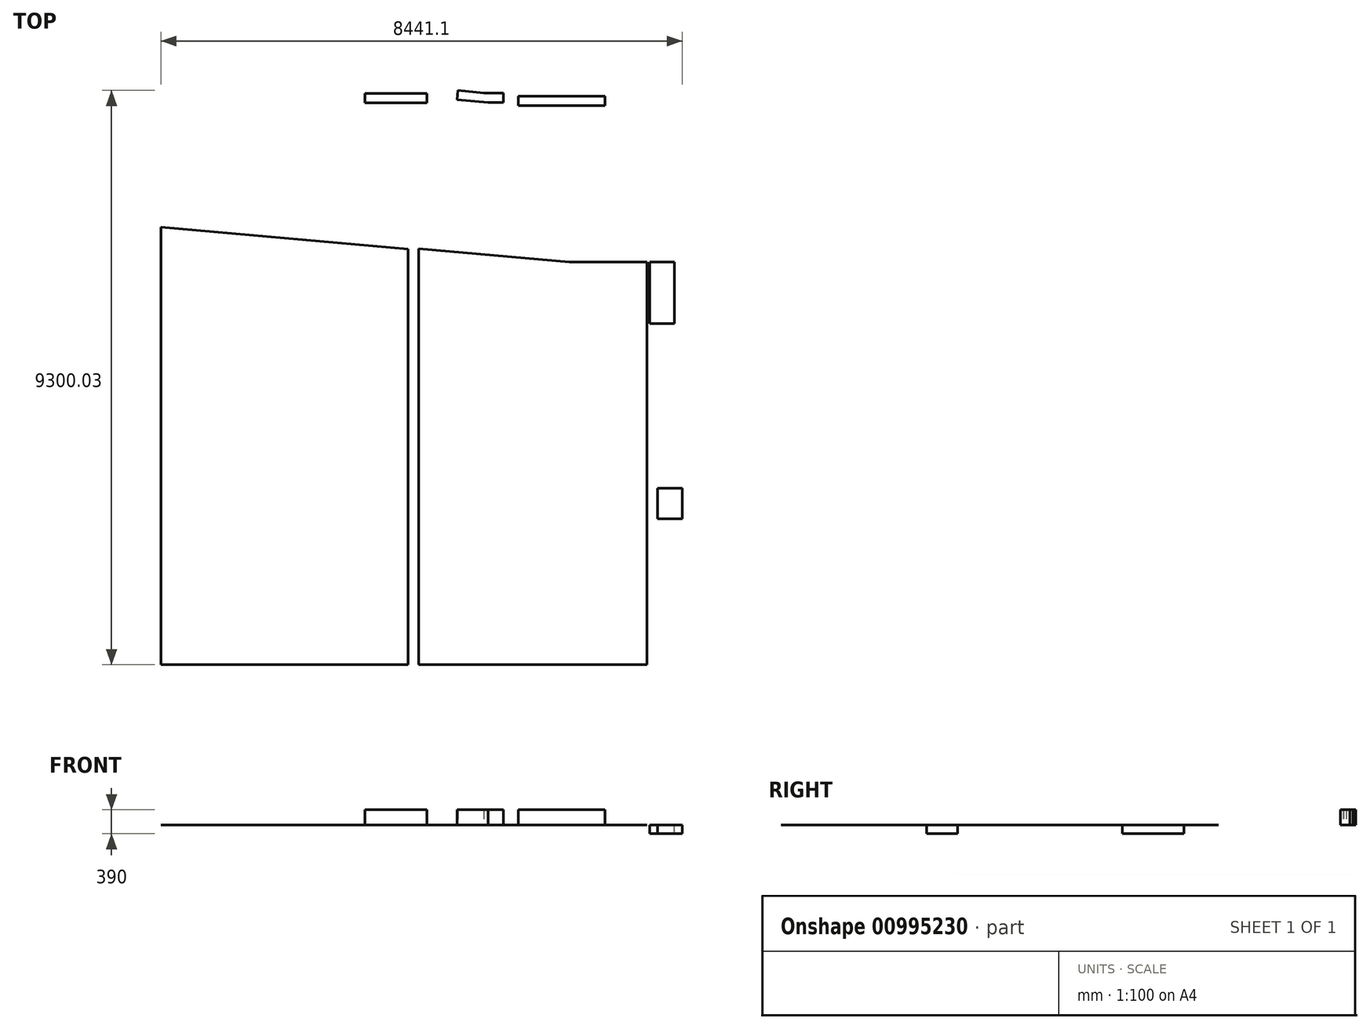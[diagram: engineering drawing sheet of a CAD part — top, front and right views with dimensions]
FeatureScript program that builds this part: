
annotation { "Feature Type Name" : "Feature", "Feature Type Description" : "" }
export const myFeature = defineFeature(function(context is Context, id is Id, definition is map)
    precondition{}
    {
        {
            var Q0;
            Q0=qCreatedBy(makeId("Top.planeOp"),FACE);
            var sketch = newSketch(context, id + "F0", { "sketchPlane" : qUnion([Q0])});
            skLineSegment(sketch, "E0.top", {"start": v(-636.14, -1695.39) * mm, "end": v(3063.86, -1695.39) * mm});
            skLineSegment(sketch, "E0.right", {"start": v(3063.86, 4827.36) * mm, "end": v(3063.86, -1695.39) * mm});
            skLineSegment(sketch, "E1.bottom", {"start": v(3108.46, 4827.36) * mm, "end": v(3508.46, 4827.36) * mm});
            skLineSegment(sketch, "E1.top", {"start": v(3108.46, 3827.36) * mm, "end": v(3508.46, 3827.36) * mm});
            skLineSegment(sketch, "E1.left", {"start": v(3108.46, 4827.36) * mm, "end": v(3108.46, 3827.36) * mm});
            skLineSegment(sketch, "E1.right", {"start": v(3508.46, 4827.36) * mm, "end": v(3508.46, 3827.36) * mm});
            skLineSegment(sketch, "E2.bottom", {"start": v(-808.16, -1695.39) * mm, "end": v(-4808.16, -1695.39) * mm});
            skLineSegment(sketch, "E2.left", {"start": v(-808.16, -1695.39) * mm, "end": v(-808.16, 5037.3) * mm});
            skLineSegment(sketch, "E2.right", {"start": v(-4808.16, -1695.39) * mm, "end": v(-4808.16, 5387.26) * mm});
            skLineSegment(sketch, "E3.bottom", {"start": v(3232.94, 1163.24) * mm, "end": v(3632.94, 1163.24) * mm});
            skLineSegment(sketch, "E3.top", {"start": v(3232.94, 663.24) * mm, "end": v(3632.94, 663.24) * mm});
            skLineSegment(sketch, "E3.left", {"start": v(3232.94, 1163.24) * mm, "end": v(3232.94, 663.24) * mm});
            skLineSegment(sketch, "E3.right", {"start": v(3632.94, 1163.24) * mm, "end": v(3632.94, 663.24) * mm});
            skLineSegment(sketch, "E4.bottom", {"start": v(979.8, 7509.1) * mm, "end": v(2379.8, 7509.1) * mm});
            skLineSegment(sketch, "E4.top", {"start": v(979.8, 7359.1) * mm, "end": v(2379.8, 7359.1) * mm});
            skLineSegment(sketch, "E4.left", {"start": v(979.8, 7509.1) * mm, "end": v(979.8, 7359.1) * mm});
            skLineSegment(sketch, "E4.right", {"start": v(2379.8, 7509.1) * mm, "end": v(2379.8, 7359.1) * mm});
            skLineSegment(sketch, "E5.bottom", {"start": v(737.73, 7411.64) * mm, "end": v(487.73, 7411.64) * mm});
            skLineSegment(sketch, "E5.top", {"start": v(737.73, 7561.64) * mm, "end": v(417.83, 7561.64) * mm});
            skLineSegment(sketch, "E5.left", {"start": v(737.73, 7411.64) * mm, "end": v(737.73, 7561.64) * mm});
            skLineSegment(sketch, "E6", {"start": v(487.73, 7411.64) * mm, "end": v(-10.37, 7455.21) * mm});
            skLineSegment(sketch, "E7", {"start": v(-10.37, 7455.21) * mm, "end": v(2.7, 7604.64) * mm});
            skLineSegment(sketch, "E8", {"start": v(2.7, 7604.64) * mm, "end": v(417.83, 7561.64) * mm});
            skLineSegment(sketch, "E9", {"start": v(1803.86, 4827.36) * mm, "end": v(-636.14, 5040.83) * mm});
            skLineSegment(sketch, "E10", {"start": v(1803.86, 4827.36) * mm, "end": v(3063.86, 4827.36) * mm});
            skLineSegment(sketch, "E11.bottom", {"start": v(-1502.82, 7554.66) * mm, "end": v(-502.82, 7554.66) * mm});
            skLineSegment(sketch, "E11.top", {"start": v(-1502.82, 7404.66) * mm, "end": v(-502.82, 7404.66) * mm});
            skLineSegment(sketch, "E11.left", {"start": v(-1502.82, 7554.66) * mm, "end": v(-1502.82, 7404.66) * mm});
            skLineSegment(sketch, "E11.right", {"start": v(-502.82, 7554.66) * mm, "end": v(-502.82, 7404.66) * mm});
            skLineSegment(sketch, "E12", {"start": v(-4808.16, 5387.26) * mm, "end": v(-808.16, 5037.3) * mm});
            skLineSegment(sketch, "E13", {"start": v(-636.14, 5040.83) * mm, "end": v(-636.14, -1695.39) * mm});
            skSolve(sketch);
        }
        {
            var Q0;
            Q0=makeQuery(id+"F0.imprint","IMPRINT",FACE,{"disambiguationData":[TD([[makeQuery(id+"F0.imprint","IMPRINT",EDGE,{"derivedFrom":sQuery(id+"F0.wireOp",EDGE,"E1.bottom")}),-1.0]])]});
            var Q1;
            Q1=makeQuery(id+"F0.imprint","IMPRINT",FACE,{"disambiguationData":[TD([[makeQuery(id+"F0.imprint","IMPRINT",EDGE,{"derivedFrom":sQuery(id+"F0.wireOp",EDGE,"E3.bottom")}),-1.0]])]});
            extrude(context, id + "F1", {"entities" : qUnion([Q0, Q1]), "oppositeDirection" : true, "depth" : 140 * mm, "offsetDistance" : 25 * mm});
        }
        {
            var Q0;
            Q0=makeQuery(id+"F0.imprint","IMPRINT",FACE,{"disambiguationData":[TD([[makeQuery(id+"F0.imprint","IMPRINT",EDGE,{"derivedFrom":sQuery(id+"F0.wireOp",EDGE,"E2.bottom")}),-1.0]])]});
            extrude(context, id + "F2", {"entities" : qUnion([Q0]), "oppositeDirection" : true, "depth" : 1 * mm, "offsetDistance" : 25 * mm});
        }
        {
            var Q0;
            Q0=sQuery(id+"F0.wireOp",EDGE,"E0.left");
            var Q1;
            Q1=sQuery(id+"F0.wireOp",EDGE,"E9");
            var Q2;
            Q2=sQuery(id+"F0.wireOp",EDGE,"E10");
            var Q3;
            Q3=sQuery(id+"F0.wireOp",EDGE,"E0.right");
            var Q4;
            Q4=sQuery(id+"F0.wireOp",EDGE,"E0.top");
            extrude(context, id + "F3", {"bodyType" : ToolBodyType.SURFACE, "surfaceEntities" : qUnion([Q0, Q1, Q2, Q3, Q4]), "depth" : 1 * mm, "offsetDistance" : 25 * mm});
        }
        {
            var Q0;
            Q0=makeQuery(id+"F0.imprint","IMPRINT",FACE,{"disambiguationData":[TD([[makeQuery(id+"F0.imprint","IMPRINT",EDGE,{"derivedFrom":sQuery(id+"F0.wireOp",EDGE,"E0.top")}),1.0]])]});
            extrude(context, id + "F4", {"entities" : qUnion([Q0]), "depth" : 1 * mm, "offsetDistance" : 25 * mm});
        }
        {
            var Q0;
            Q0=makeQuery(id+"F3.opExtrude","SWEPT_BODY",BODY,{"disambiguationData":[OSD([sQuery(id+"F0.wireOp",EDGE,"E0.top")])]});
            deleteBodies(context, id + "F5", {"entities" : qUnion([Q0])});
        }
        {
            var Q0;
            Q0=makeQuery(id+"F0.imprint","IMPRINT",FACE,{"disambiguationData":[TD([[makeQuery(id+"F0.imprint","IMPRINT",EDGE,{"derivedFrom":sQuery(id+"F0.wireOp",EDGE,"E11.bottom")}),-1.0]])]});
            var Q1;
            Q1=makeQuery(id+"F0.imprint","IMPRINT",FACE,{"disambiguationData":[TD([[makeQuery(id+"F0.imprint","IMPRINT",EDGE,{"derivedFrom":sQuery(id+"F0.wireOp",EDGE,"E5.bottom")}),-1.0]])]});
            var Q2;
            Q2=makeQuery(id+"F0.imprint","IMPRINT",FACE,{"disambiguationData":[TD([[makeQuery(id+"F0.imprint","IMPRINT",EDGE,{"derivedFrom":sQuery(id+"F0.wireOp",EDGE,"E4.bottom")}),-1.0]])]});
            extrude(context, id + "F6", {"entities" : qUnion([Q0, Q1, Q2]), "depth" : 250 * mm, "offsetDistance" : 25 * mm});
        }
    });
